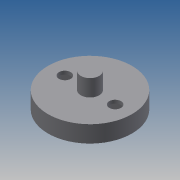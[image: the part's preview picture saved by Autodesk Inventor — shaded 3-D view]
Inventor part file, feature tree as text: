
AUTODESK INVENTOR PART (.ipt)
format: ipt  version: 2013 (Build 170138000, 138)  size: 108,032 bytes
history: native  units: mm
features: extrude x4, sketch x4
ambient origin geometry x8: Origin, YZ Plane, XZ Plane, XY Plane, X Axis, Y Axis, Z Axis, Center Point
bodies: Solid1 (feature_tree)
feature tree (8):
  extrude  "Extrusion1"  Depth=5.0mm TaperAngle=0.0deg
  extrude  "Extrusion2"  Depth=5.0mm TaperAngle=0.0deg
  extrude  "Extrusion3"  Depth=7.5mm
  extrude  "Extrusion4"  Depth=5.0mm TaperAngle=0.0deg
  sketch  "Sketch1"  dims[d0=25.0mm d2=5.0mm d3=0.0mm]
  sketch  "Sketch2"  dims[d4=5.5mm d6=5.0mm d7=0.0mm]
  sketch  "Sketch3"  dims[d8=7.5mm d9=7.5mm]
  sketch  "Sketch4"  dims[d10=3.5mm d11=5.0mm d12=0.0mm d13=5.5mm d14=4.0mm d15=0.0mm]
